# Revit family: Hekatron_Brandmeldetechnik_HAT 155 F UP_DE_23.01
name_source: partatom
category: Brandmelder
revit_build: Autodesk Revit 2018 (Build: 20170223_1515(x64)
units: mm (PartAtom-declared; Revit-internal decimal feet)

## family parameters
Basisbauteil = Fläche
Beim Laden mit Abzugskörper schneiden = Nein
Bemaßung runder Anschluss = Durchmesser verwenden
Beschriftungsausrichtung beibehalten = Ja
Gemeinsam genutzt = Nein
OmniClass-Nummer = 23.85.30.21
OmniClass-Titel = Environmental Detection/Registration
Raumberechnungspunkt = Nein
Teiletyp = Normal

## types (1)
- HAT 155 F UP
    Beschreibung = Funk-Handtaster 155 F Unterputz
    Betriebsspannung = 3 V DC
    Breite (mm) = 81.0
    EG-Konformitaetszertifikat / Zertifikat der Leistungsbestaendigkeit = 1772-CPR-200342
    Farbe = weiß ähnlich RAL 9010, rot ähnlich RAL 3000
    Hersteller = Hekatron
    Hoehe (mm) = 81.0
    Kabeleinführung = hinten
    Leistungserklaerung (DoP) = CRP-31-20-002
    Link zu Ausschreibungstext = https://www.meinhplus.de
    Link zu Produktinformation = https://www.hekatron-brandschutz.de
    Link zu ausschreiben.de = https://ausschreiben.de
    Link zum Datenblatt = https://www.hekatron-brandschutz.de
    Material = PC-ABS
    Modell = HAT 155 F UP
    Montageart = Unterputz
    Nettogewicht (g) = 127.0
    Schutzart = IP 20
    Tiefe (mm) = 21.0
    Typenkommentare = Handauslösetaster 155 Funk Unterputz
    UB A&S Artikel Nummer = 31-4100022-01-01
    URL = www.hekatron-brandschutz.de
    Version des BIM Objektes = 23.01
    Vorgabe-Ansicht = 1200 mm
    Zulaessige Umgebungstemperatur = -30 °C bis 70 °C
    Zulassungen nach EN 54 = 54-18, 54-25

## geometry (parser evidence)
native form markers: Sweep x2
no freeform markers — native parametric forms only
